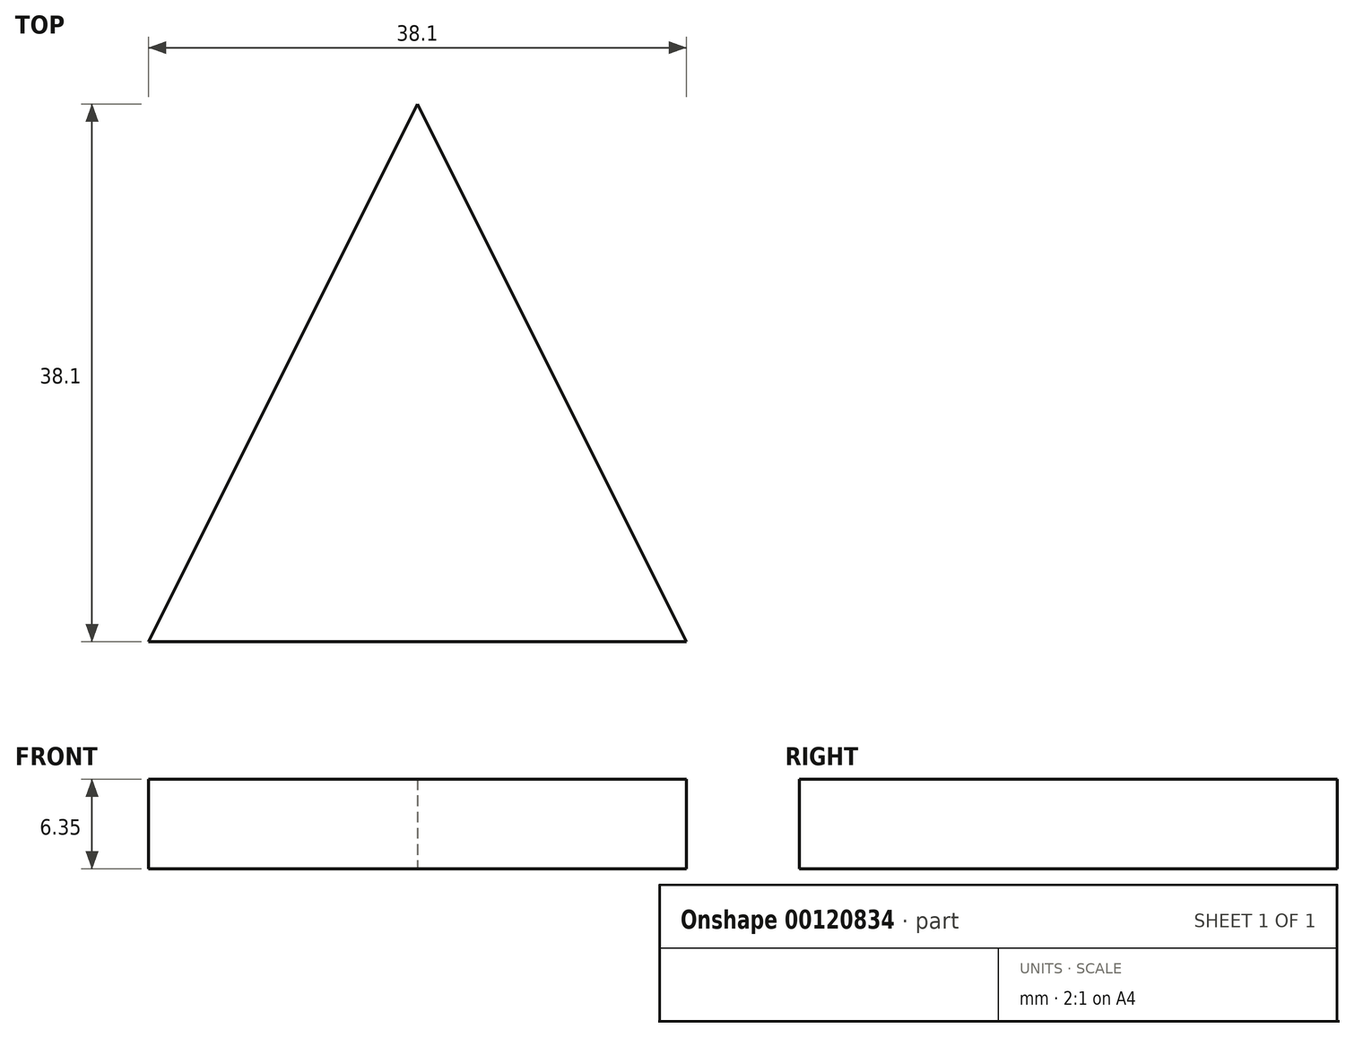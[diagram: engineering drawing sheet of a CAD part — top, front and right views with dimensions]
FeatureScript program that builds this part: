
annotation { "Feature Type Name" : "Feature", "Feature Type Description" : "" }
export const myFeature = defineFeature(function(context is Context, id is Id, definition is map)
    precondition{}
    {
        {
            var Q0;
            Q0=qCreatedBy(makeId("Top.planeOp"),FACE);
            var sketch = newSketch(context, id + "F0", { "sketchPlane" : qUnion([Q0])});
            skLineSegment(sketch, "E0", {"start": v(0, 0) * mm, "end": v(0, 38.1) * mm, "construction": true});
            skLineSegment(sketch, "E1", {"start": v(-19.05, 0) * mm, "end": v(19.05, 0) * mm});
            skLineSegment(sketch, "E2", {"start": v(19.05, 0) * mm, "end": v(0, 38.1) * mm});
            skLineSegment(sketch, "E3", {"start": v(0, 38.1) * mm, "end": v(-19.05, 0) * mm});
            skSolve(sketch);
        }
        {
            var Q0;
            Q0 = qSketchRegion(id + "F0", true);
            extrude(context, id + "F1", {"entities" : qUnion([Q0]), "depth" : 6.35 * mm});
        }
    });
